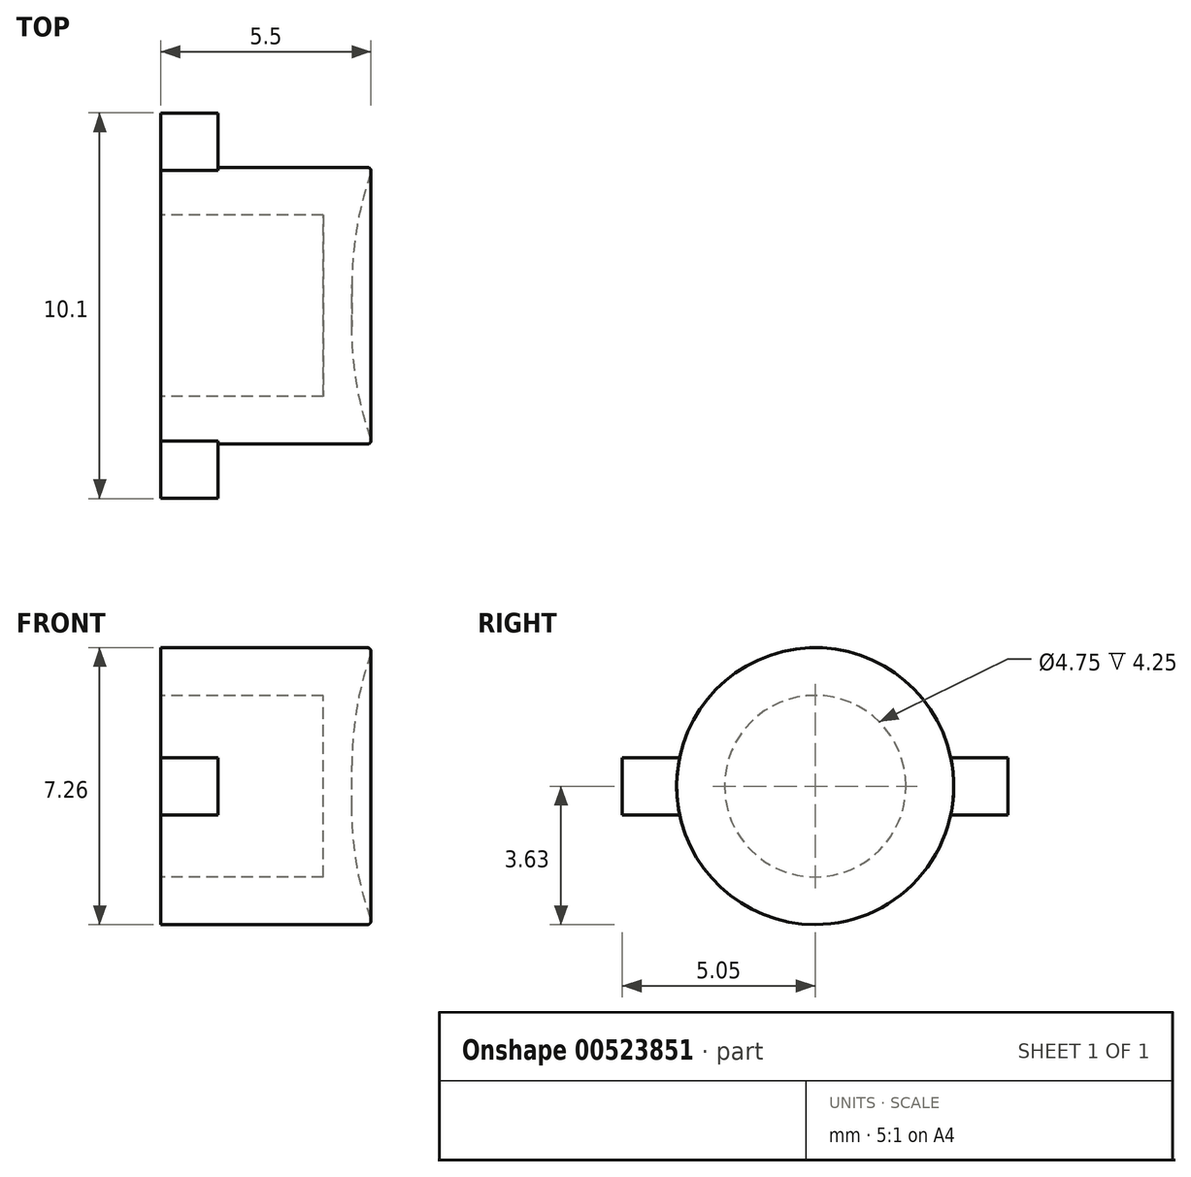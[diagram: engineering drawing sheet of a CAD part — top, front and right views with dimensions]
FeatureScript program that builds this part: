
annotation { "Feature Type Name" : "Feature", "Feature Type Description" : "" }
export const myFeature = defineFeature(function(context is Context, id is Id, definition is map)
    precondition{}
    {
        {
            var Q0;
            Q0=qCreatedBy(makeId("Right.planeOp"),FACE);
            var sketch = newSketch(context, id + "F0", { "sketchPlane" : qUnion([Q0])});
            skCircle(sketch, "E0", {"center": v(0, 0) * mm, "radius": 3.62 * mm});
            skSolve(sketch);
        }
        {
            var Q0;
            Q0=makeQuery(id+"F0.imprint","IMPRINT",FACE,{"disambiguationData":[TD([[makeQuery(id+"F0.imprint","IMPRINT",EDGE,{"derivedFrom":sQuery(id+"F0.wireOp",EDGE,"E0")}),1.0]])]});
            extrude(context, id + "F1", {"entities" : qUnion([Q0]), "endBound" : BoundingType.SYMMETRIC, "depth" : 5.5 * mm, "offsetDistance" : 25 * mm});
        }
        {
            var Q0;
            Q0=makeQuery(id+"F1.opExtrude","CAP_FACE",FACE,{"disambiguationData":[OSD([sQuery(id+"F0.wireOp",EDGE,"E0")])],"isStart":true});
            shell(context, id + "F2", {"entities" : qUnion([Q0]), "thickness" : 1.25 * mm});
        }
        {
            var Q0;
            Q0=makeQuery(id+"F1.opExtrude","CAP_FACE",FACE,{"disambiguationData":[OSD([sQuery(id+"F0.wireOp",EDGE,"E0")])],"isStart":true});
            var sketch = newSketch(context, id + "F3", { "sketchPlane" : qUnion([Q0])});
            skLineSegment(sketch, "E1.left", {"start": v(5.05, -0.75) * mm, "end": v(5.05, 0.75) * mm});
            skLineSegment(sketch, "E2.left", {"start": v(-5.05, 0.75) * mm, "end": v(-5.05, -0.75) * mm});
            skLineSegment(sketch, "E3", {"start": v(5.05, 0.75) * mm, "end": v(3.55, 0.75) * mm});
            skLineSegment(sketch, "E4", {"start": v(5.05, -0.75) * mm, "end": v(3.55, -0.75) * mm});
            skArc(sketch, "E5", {"start": v(-3.55, 0.75) * mm, "mid": v(-3.63, 0) * mm, "end": v(-3.55, -0.75) * mm});
            skLineSegment(sketch, "E6", {"start": v(-5.05, 0.75) * mm, "end": v(-3.55, 0.75) * mm});
            skLineSegment(sketch, "E7", {"start": v(-5.05, -0.75) * mm, "end": v(-3.55, -0.75) * mm});
            skArc(sketch, "E8.trimOffspring", {"start": v(3.55, -0.75) * mm, "mid": v(3.63, 0) * mm, "end": v(3.55, 0.75) * mm});
            skPoint(sketch, "E9", {"position": v(5.05, 0) * mm});
            skPoint(sketch, "E10", {"position": v(-5.05, 0) * mm});
            skSolve(sketch);
        }
        {
            var Q0;
            Q0=qSketchRegion(id+"F3",true);
            extrude(context, id + "F4", {"entities" : qUnion([Q0]), "operationType" : NewBodyOperationType.ADD, "oppositeDirection" : true, "depth" : 1.5 * mm, "offsetDistance" : 25 * mm});
        }
        {
            var Q0;
            Q0=makeQuery(id+"F1.opExtrude","CAP_FACE",FACE,{"disambiguationData":[OSD([sQuery(id+"F0.wireOp",EDGE,"E0")])],"isStart":false});
            var sketch = newSketch(context, id + "F5", { "sketchPlane" : qUnion([Q0])});
            skCircle(sketch, "E11", {"center": v(0, 0) * mm, "radius": 3.5 * mm});
            skSolve(sketch);
        }
        {
            var Q0;
            Q0 = qSketchRegion(id + "F5", true);
            extrude(context, id + "F6", {"entities" : qUnion([Q0]), "operationType" : NewBodyOperationType.REMOVE, "oppositeDirection" : true, "depth" : .5 * mm, "offsetDistance" : 25 * mm});
        }
        {
            var Q0;
            Q0=makeQuery(id+"F6.boolean.opBoolean","COPY",FACE,{"derivedFrom":makeQuery(id+"F6.opExtrude","CAP_FACE",FACE,{"disambiguationData":[OSD([sQuery(id+"F5.wireOp",EDGE,"E11")])],"isStart":false})});
            fillet(context, id + "F7", {"entities" : qUnion([Q0]), "radius" : 9 * mm, "tangentPropagation" : true, "allowEdgeOverflow" : false});
        }
        {
            var Q0;
            Q0=makeQuery(id+"F7.opFillet","BLEND_EDGE",EDGE,{"blendedFrom":[makeQuery(id+"F6.boolean.opBoolean","COPY",EDGE,{"derivedFrom":makeQuery(id+"F6.opExtrude","CAP_EDGE",EDGE,{"disambiguationData":[OSD([sQuery(id+"F5.wireOp",EDGE,"E11")])],"isStart":false})}),makeQuery(id+"F1.opExtrude","CAP_FACE",FACE,{"disambiguationData":[OSD([sQuery(id+"F0.wireOp",EDGE,"E0")])],"isStart":false})],"blendedInto":[makeQuery(id+"F1.opExtrude","CAP_FACE",FACE,{"disambiguationData":[OSD([sQuery(id+"F0.wireOp",EDGE,"E0")])],"isStart":false})]});
            var Q1;
            Q1=makeQuery(id+"F1.opExtrude","CAP_EDGE",EDGE,{"disambiguationData":[OSD([sQuery(id+"F0.wireOp",EDGE,"E0")])],"isStart":false});
            fillet(context, id + "F8", {"entities" : qUnion([Q0, Q1]), "radius" : .1 * mm, "tangentPropagation" : true, "allowEdgeOverflow" : false});
        }
    });
